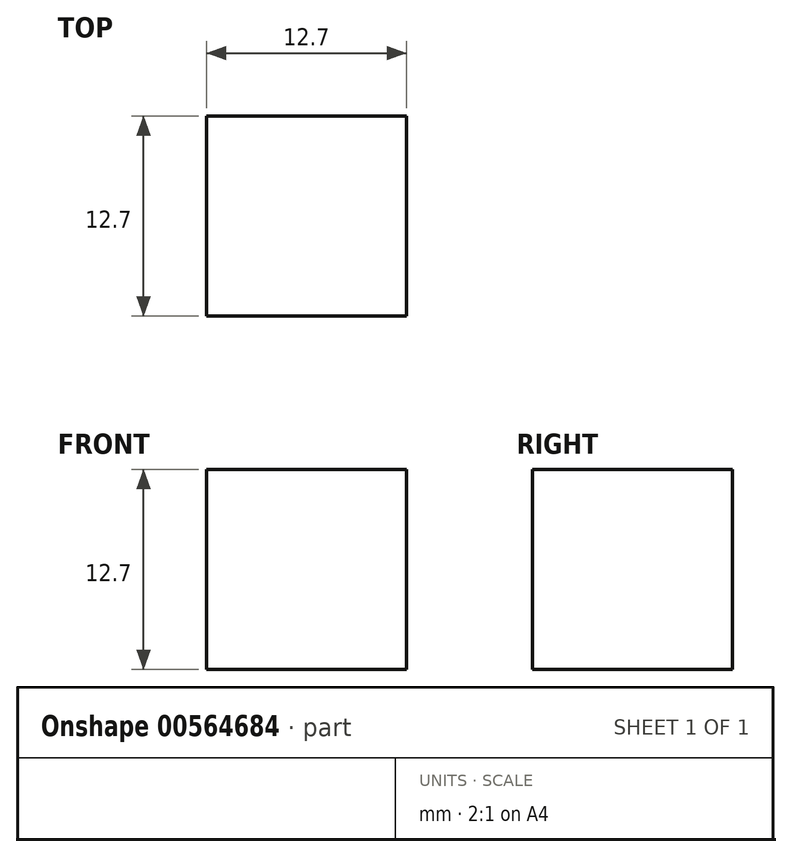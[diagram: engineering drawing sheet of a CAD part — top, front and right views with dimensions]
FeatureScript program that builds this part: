
annotation { "Feature Type Name" : "Feature", "Feature Type Description" : "" }
export const myFeature = defineFeature(function(context is Context, id is Id, definition is map)
    precondition{}
    {
        {
            var Q0;
            Q0=qCreatedBy(makeId("Top.planeOp"),FACE);
            var sketch = newSketch(context, id + "F0", { "sketchPlane" : qUnion([Q0])});
            skLineSegment(sketch, "E0.bottom", {"start": v(-12.7, 12.7) * mm, "end": v(12.7, 12.7) * mm, "construction": true});
            skLineSegment(sketch, "E0.top", {"start": v(-12.7, -12.7) * mm, "end": v(12.7, -12.7) * mm, "construction": true});
            skLineSegment(sketch, "E0.left", {"start": v(-12.7, 12.7) * mm, "end": v(-12.7, -12.7) * mm, "construction": true});
            skLineSegment(sketch, "E0.right", {"start": v(12.7, 12.7) * mm, "end": v(12.7, -12.7) * mm, "construction": true});
            skPoint(sketch, "E0.middle", {"position": v(0, 0) * mm});
            skLineSegment(sketch, "E1.bottom", {"start": v(6.35, 6.35) * mm, "end": v(-6.35, 6.35) * mm});
            skLineSegment(sketch, "E1.top", {"start": v(6.35, -6.35) * mm, "end": v(-6.35, -6.35) * mm});
            skLineSegment(sketch, "E1.left", {"start": v(6.35, 6.35) * mm, "end": v(6.35, -6.35) * mm});
            skLineSegment(sketch, "E1.right", {"start": v(-6.35, 6.35) * mm, "end": v(-6.35, -6.35) * mm});
            skSolve(sketch);
        }
        {
            var Q0;
            Q0 = qSketchRegion(id + "F0", true);
            extrude(context, id + "F1", {"entities" : qUnion([Q0]), "depth" : 12.7 * mm, "offsetDistance" : 25.4 * mm});
        }
    });
